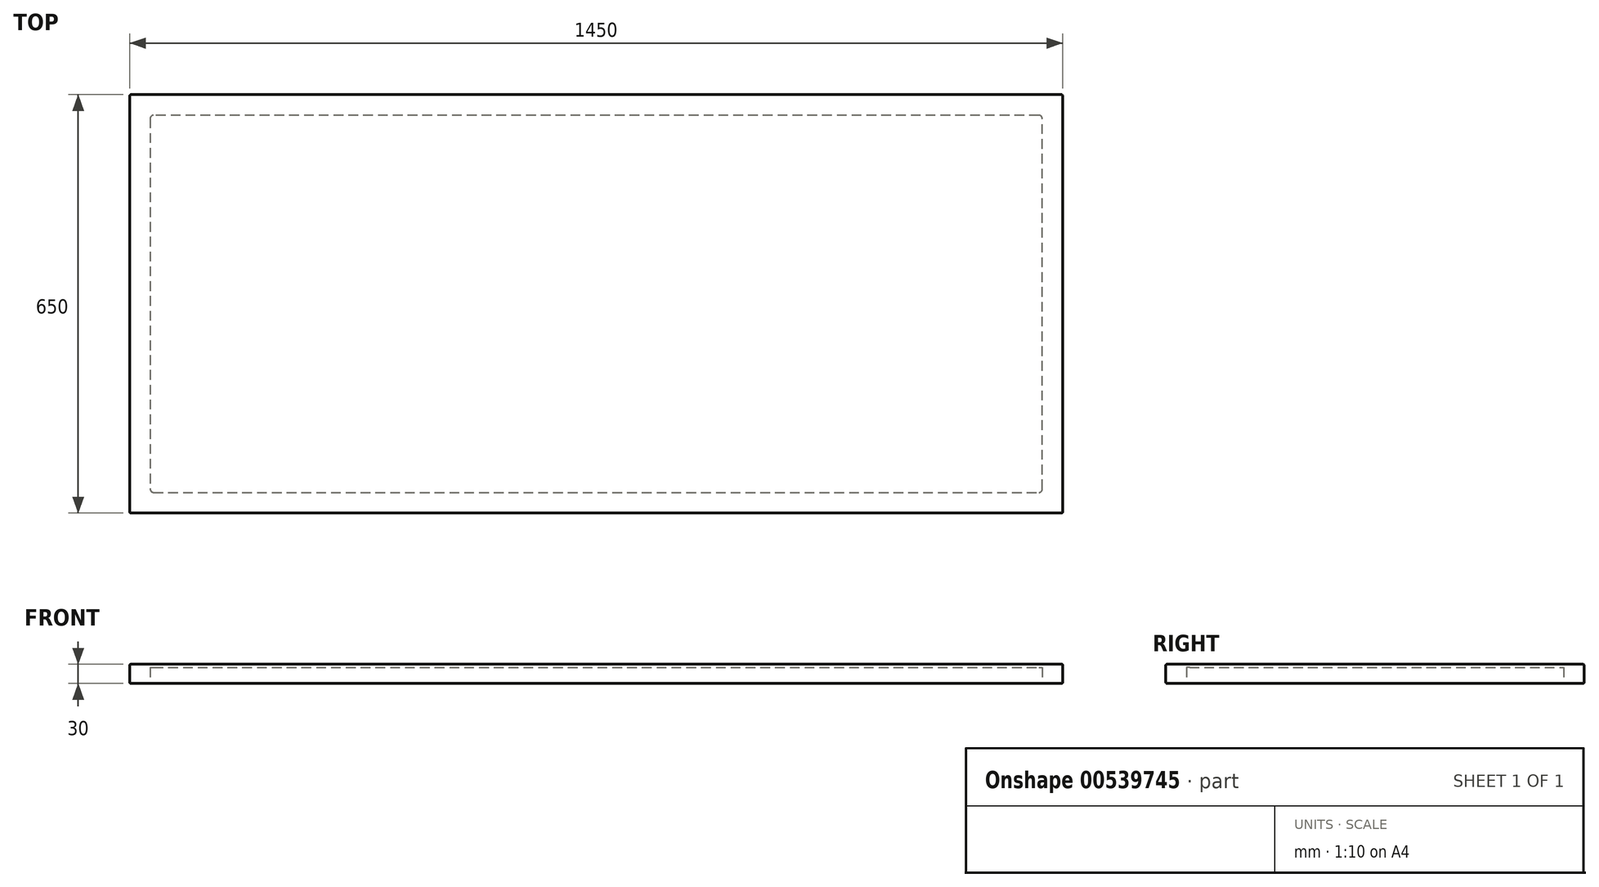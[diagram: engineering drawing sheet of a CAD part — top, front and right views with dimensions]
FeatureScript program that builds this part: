
annotation { "Feature Type Name" : "Feature", "Feature Type Description" : "" }
export const myFeature = defineFeature(function(context is Context, id is Id, definition is map)
    precondition{}
    {
        {
            var Q0;
            Q0=qCreatedBy(makeId("Top.planeOp"),FACE);
            var sketch = newSketch(context, id + "F0", { "sketchPlane" : qUnion([Q0])});
            skLineSegment(sketch, "E0.bottom", {"start": v(0, 0) * mm, "end": v(1450, 0) * mm});
            skLineSegment(sketch, "E0.top", {"start": v(0, 650) * mm, "end": v(1450, 650) * mm});
            skLineSegment(sketch, "E0.left", {"start": v(0, 0) * mm, "end": v(0, 650) * mm});
            skLineSegment(sketch, "E0.right", {"start": v(1450, 0) * mm, "end": v(1450, 650) * mm});
            skSolve(sketch);
        }
        {
            var Q0;
            Q0=makeQuery(id+"F0.imprint","IMPRINT",FACE,{"disambiguationData":[TD([[makeQuery(id+"F0.imprint","IMPRINT",EDGE,{"derivedFrom":sQuery(id+"F0.wireOp",EDGE,"E0.bottom")}),1.0]])]});
            extrude(context, id + "F1", {"entities" : qUnion([Q0]), "oppositeDirection" : true, "depth" : 30 * mm, "offsetDistance" : 25 * mm});
        }
        {
            var Q0;
            Q0=makeQuery(id+"F1.opExtrude","SWEPT_EDGE",EDGE,{"disambiguationData":[OSD([sQuery(id+"F0.wireOp",EDGE,"E0.top"),sQuery(id+"F0.wireOp",EDGE,"E0.left")])]});
            var Q1;
            Q1=makeQuery(id+"F1.opExtrude","CAP_EDGE",EDGE,{"disambiguationData":[OSD([sQuery(id+"F0.wireOp",EDGE,"E0.top")])],"isStart":false});
            var Q2;
            Q2=makeQuery(id+"F1.opExtrude","CAP_FACE",FACE,{"disambiguationData":[OSD([sQuery(id+"F0.wireOp",EDGE,"E0.bottom"),sQuery(id+"F0.wireOp",EDGE,"E0.top"),sQuery(id+"F0.wireOp",EDGE,"E0.left"),sQuery(id+"F0.wireOp",EDGE,"E0.right")])],"isStart":false});
            var Q3;
            Q3=makeQuery(id+"F1.opExtrude","CAP_FACE",FACE,{"disambiguationData":[OSD([sQuery(id+"F0.wireOp",EDGE,"E0.bottom"),sQuery(id+"F0.wireOp",EDGE,"E0.top"),sQuery(id+"F0.wireOp",EDGE,"E0.left"),sQuery(id+"F0.wireOp",EDGE,"E0.right")])],"isStart":true});
            var Q4;
            Q4=makeQuery(id+"F1.opExtrude","SWEPT_EDGE",EDGE,{"disambiguationData":[OSD([sQuery(id+"F0.wireOp",EDGE,"E0.bottom"),sQuery(id+"F0.wireOp",EDGE,"E0.left")])]});
            var Q5;
            Q5=makeQuery(id+"F1.opExtrude","SWEPT_EDGE",EDGE,{"disambiguationData":[OSD([sQuery(id+"F0.wireOp",EDGE,"E0.bottom"),sQuery(id+"F0.wireOp",EDGE,"E0.right")])]});
            var Q6;
            Q6=makeQuery(id+"F1.opExtrude","SWEPT_EDGE",EDGE,{"disambiguationData":[OSD([sQuery(id+"F0.wireOp",EDGE,"E0.top"),sQuery(id+"F0.wireOp",EDGE,"E0.right")])]});
            fillet(context, id + "F2", {"entities" : qUnion([Q0, Q1, Q2, Q3, Q4, Q5, Q6]), "radius" : 2 * mm, "tangentPropagation" : true, "allowEdgeOverflow" : false});
        }
        {
            var Q0;
            Q0=makeQuery(id+"F1.opExtrude","CAP_FACE",FACE,{"disambiguationData":[OSD([sQuery(id+"F0.wireOp",EDGE,"E0.bottom"),sQuery(id+"F0.wireOp",EDGE,"E0.top"),sQuery(id+"F0.wireOp",EDGE,"E0.left"),sQuery(id+"F0.wireOp",EDGE,"E0.right")])],"isStart":false});
            var sketch = newSketch(context, id + "F3", { "sketchPlane" : qUnion([Q0])});
            skLineSegment(sketch, "E1.0", {"start": v(1418, -32) * mm, "end": v(1418, -618) * mm});
            skLineSegment(sketch, "E1.1", {"start": v(1418, -618) * mm, "end": v(32, -618) * mm});
            skLineSegment(sketch, "E1.2", {"start": v(32, -618) * mm, "end": v(32, -32) * mm});
            skLineSegment(sketch, "E1.3", {"start": v(32, -32) * mm, "end": v(1418, -32) * mm});
            skLineSegment(sketch, "E2.0", {"start": v(1443, -7) * mm, "end": v(1443, -643) * mm});
            skLineSegment(sketch, "E2.1", {"start": v(1443, -643) * mm, "end": v(7, -643) * mm});
            skLineSegment(sketch, "E2.2", {"start": v(7, -643) * mm, "end": v(7, -7) * mm});
            skLineSegment(sketch, "E2.3", {"start": v(7, -7) * mm, "end": v(1443, -7) * mm});
            skSolve(sketch);
        }
        {
            var Q0;
            Q0=makeQuery(id+"F3.imprint","IMPRINT",FACE,{"disambiguationData":[TD([[makeQuery(id+"F3.imprint","IMPRINT",EDGE,{"derivedFrom":sQuery(id+"F3.wireOp",EDGE,"E1.0")}),-1.0]])]});
            extrude(context, id + "F4", {"entities" : qUnion([Q0]), "operationType" : NewBodyOperationType.REMOVE, "oppositeDirection" : true, "depth" : 25 * mm, "offsetDistance" : 25 * mm});
        }
        {
            var Q0;
            Q0=makeQuery(id+"F4.boolean.opBoolean","COPY",EDGE,{"derivedFrom":makeQuery(id+"F4.opExtrude","SWEPT_EDGE",EDGE,{"disambiguationData":[OSD([sQuery(id+"F3.wireOp",EDGE,"E1.0"),sQuery(id+"F3.wireOp",EDGE,"E1.1")])]})});
            var Q1;
            Q1=makeQuery(id+"F4.boolean.opBoolean","COPY",EDGE,{"derivedFrom":makeQuery(id+"F4.opExtrude","SWEPT_EDGE",EDGE,{"disambiguationData":[OSD([sQuery(id+"F3.wireOp",EDGE,"E1.0"),sQuery(id+"F3.wireOp",EDGE,"E1.3")])]})});
            var Q2;
            Q2=makeQuery(id+"F4.boolean.opBoolean","COPY",EDGE,{"derivedFrom":makeQuery(id+"F4.opExtrude","SWEPT_EDGE",EDGE,{"disambiguationData":[OSD([sQuery(id+"F3.wireOp",EDGE,"E1.2"),sQuery(id+"F3.wireOp",EDGE,"E1.3")])]})});
            var Q3;
            Q3=makeQuery(id+"F4.boolean.opBoolean","COPY",EDGE,{"derivedFrom":makeQuery(id+"F4.opExtrude","CAP_EDGE",EDGE,{"disambiguationData":[OSD([sQuery(id+"F3.wireOp",EDGE,"E1.2")])],"isStart":true})});
            var Q4;
            Q4=makeQuery(id+"F4.boolean.opBoolean","COPY",EDGE,{"derivedFrom":makeQuery(id+"F4.opExtrude","CAP_EDGE",EDGE,{"disambiguationData":[OSD([sQuery(id+"F3.wireOp",EDGE,"E1.0")])],"isStart":true})});
            var Q5;
            Q5=makeQuery(id+"F4.boolean.opBoolean","COPY",EDGE,{"derivedFrom":makeQuery(id+"F4.opExtrude","SWEPT_EDGE",EDGE,{"disambiguationData":[OSD([sQuery(id+"F3.wireOp",EDGE,"E1.1"),sQuery(id+"F3.wireOp",EDGE,"E1.2")])]})});
            fillet(context, id + "F5", {"entities" : qUnion([Q0, Q1, Q2, Q3, Q4, Q5]), "radius" : 5 * mm, "tangentPropagation" : true, "allowEdgeOverflow" : false});
        }
    });
